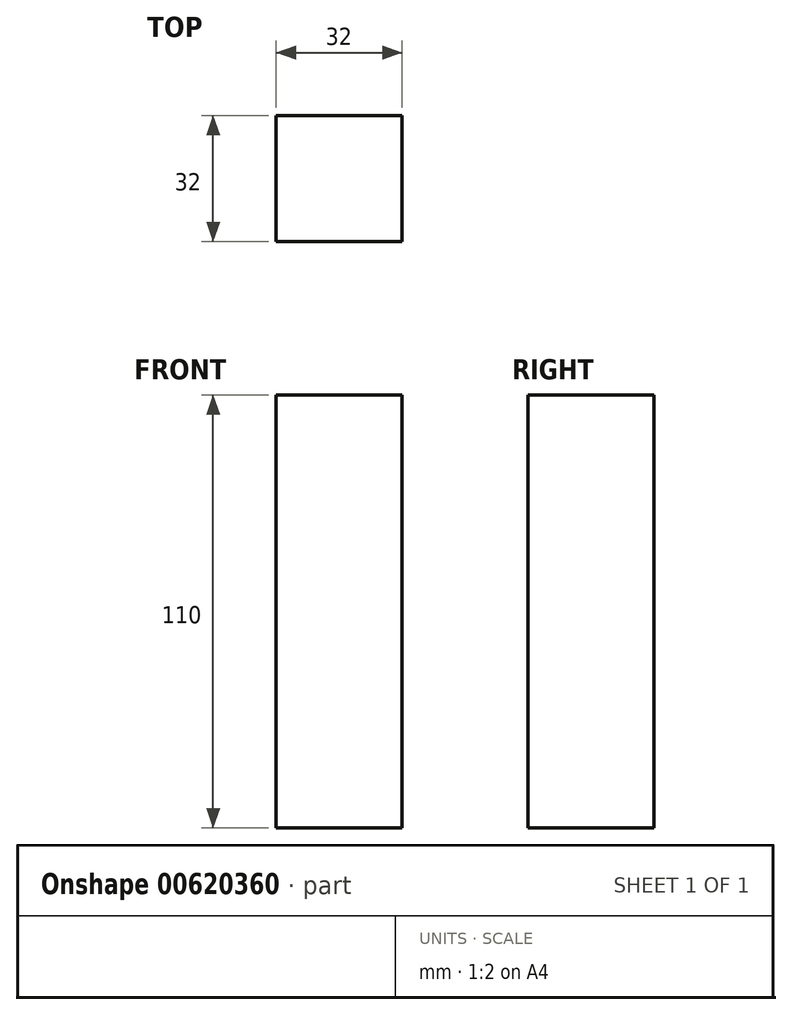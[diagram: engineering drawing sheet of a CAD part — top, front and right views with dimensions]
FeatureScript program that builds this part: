
annotation { "Feature Type Name" : "Feature", "Feature Type Description" : "" }
export const myFeature = defineFeature(function(context is Context, id is Id, definition is map)
    precondition{}
    {
        {
            var Q0;
            Q0=qCreatedBy(makeId("Front.planeOp"),FACE);
            var sketch = newSketch(context, id + "F0", { "sketchPlane" : qUnion([Q0])});
            skLineSegment(sketch, "E0", {"start": v(0, -54.37) * mm, "end": v(0, 55.63) * mm});
            skLineSegment(sketch, "E1", {"start": v(0, 55.63) * mm, "end": v(32, 55.63) * mm});
            skLineSegment(sketch, "E2", {"start": v(32, 55.63) * mm, "end": v(32, -54.37) * mm});
            skLineSegment(sketch, "E3", {"start": v(32, -54.37) * mm, "end": v(0, -54.37) * mm});
            skSolve(sketch);
        }
        {
            var Q0;
            Q0=makeQuery(id+"F0.imprint","IMPRINT",FACE,{"disambiguationData":[TD([[makeQuery(id+"F0.imprint","IMPRINT",EDGE,{"derivedFrom":sQuery(id+"F0.wireOp",EDGE,"E0")}),-1.0]])]});
            extrude(context, id + "F1", {"entities" : qUnion([Q0]), "depth" : 32 * mm, "offsetDistance" : 25 * mm});
        }
    });
